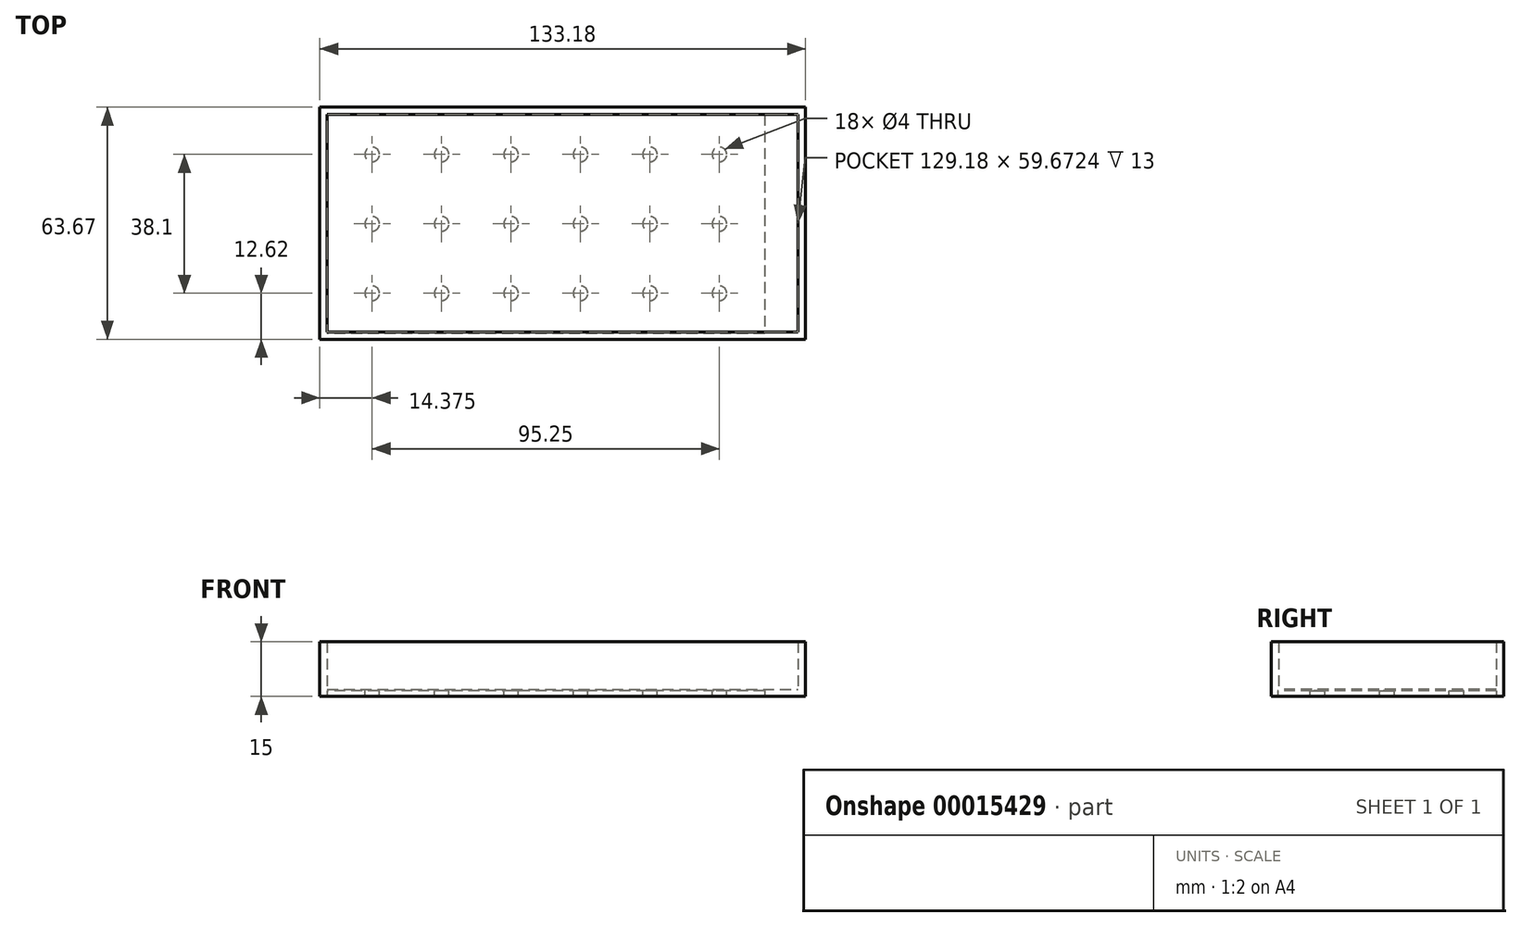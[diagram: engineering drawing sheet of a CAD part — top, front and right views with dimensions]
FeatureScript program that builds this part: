
annotation { "Feature Type Name" : "Feature", "Feature Type Description" : "" }
export const myFeature = defineFeature(function(context is Context, id is Id, definition is map)
    precondition{}
    {
        {
            var Q0;
            Q0=qCreatedBy(makeId("Top.planeOp"),FACE);
            var sketch = newSketch(context, id + "F0", { "sketchPlane" : qUnion([Q0])});
            skLineSegment(sketch, "E0.rect.bottom", {"start": v(60, 30) * mm, "end": v(-60, 30) * mm});
            skLineSegment(sketch, "E0.rect.top", {"start": v(60, -30) * mm, "end": v(-60, -30) * mm});
            skLineSegment(sketch, "E0.rect.left", {"start": v(60, 30) * mm, "end": v(60, -30) * mm});
            skLineSegment(sketch, "E0.rect.right", {"start": v(-60, 30) * mm, "end": v(-60, -30) * mm});
            skPoint(sketch, "E0.rect.middle", {"position": v(0, 0) * mm});
            skSolve(sketch);
        }
        {
            var Q0;
            Q0=qSketchRegion(id+"F0",true);
            extrude(context, id + "F1", {"entities" : qUnion([Q0]), "depth" : 1.6 * mm});
        }
        {
            var Q0;
            Q0=makeQuery(id+"F1.opExtrude","CAP_FACE",FACE,{"disambiguationData":[OSD([sQuery(id+"F0.wireOp",EDGE,"E0.rect.bottom"),sQuery(id+"F0.wireOp",EDGE,"E0.rect.top"),sQuery(id+"F0.wireOp",EDGE,"E0.rect.left"),sQuery(id+"F0.wireOp",EDGE,"E0.rect.right")])],"isStart":false});
            var sketch = newSketch(context, id + "F2", { "sketchPlane" : qUnion([Q0])});
            skCircle(sketch, "E1", {"center": v(-47.62, 19.05) * mm, "radius": 2 * mm});
            skCircle(sketch, "E2.0.1.0", {"center": v(-47.62, 0) * mm, "radius": 2 * mm});
            skCircle(sketch, "E2.0.2.0", {"center": v(-47.62, -19.05) * mm, "radius": 2 * mm});
            skCircle(sketch, "E2.1.0.0", {"center": v(-28.57, 19.05) * mm, "radius": 2 * mm});
            skCircle(sketch, "E2.1.1.0", {"center": v(-28.57, 0) * mm, "radius": 2 * mm});
            skCircle(sketch, "E2.1.2.0", {"center": v(-28.57, -19.05) * mm, "radius": 2 * mm});
            skCircle(sketch, "E2.2.0.0", {"center": v(-9.52, 19.05) * mm, "radius": 2 * mm});
            skCircle(sketch, "E2.2.1.0", {"center": v(-9.52, 0) * mm, "radius": 2 * mm});
            skCircle(sketch, "E2.2.2.0", {"center": v(-9.52, -19.05) * mm, "radius": 2 * mm});
            skCircle(sketch, "E2.3.0.0", {"center": v(9.53, 19.05) * mm, "radius": 2 * mm});
            skCircle(sketch, "E2.3.1.0", {"center": v(9.53, 0) * mm, "radius": 2 * mm});
            skCircle(sketch, "E2.3.2.0", {"center": v(9.53, -19.05) * mm, "radius": 2 * mm});
            skCircle(sketch, "E2.4.0.0", {"center": v(28.58, 19.05) * mm, "radius": 2 * mm});
            skCircle(sketch, "E2.4.1.0", {"center": v(28.58, 0) * mm, "radius": 2 * mm});
            skCircle(sketch, "E2.4.2.0", {"center": v(28.58, -19.05) * mm, "radius": 2 * mm});
            skCircle(sketch, "E2.5.0.0", {"center": v(47.62, 19.05) * mm, "radius": 2 * mm});
            skCircle(sketch, "E2.5.1.0", {"center": v(47.62, 0) * mm, "radius": 2 * mm});
            skCircle(sketch, "E2.5.2.0", {"center": v(47.62, -19.05) * mm, "radius": 2 * mm});
            skLineSegment(sketch, "E2.direction1", {"start": v(-47.62, 19.05) * mm, "end": v(-28.57, 19.05) * mm, "construction": true});
            skLineSegment(sketch, "E2.direction2", {"start": v(-47.62, 19.05) * mm, "end": v(-47.62, 0) * mm, "construction": true});
            skSolve(sketch);
        }
        {
            var Q0;
            Q0=qSketchRegion(id+"F2",true);
            extrude(context, id + "F3", {"entities" : qUnion([Q0]), "operationType" : NewBodyOperationType.REMOVE, "oppositeDirection" : true, "depth" : 25 * mm});
        }
        {
            var Q0;
            Q0=qCreatedBy(makeId("Top.planeOp"),FACE);
            var sketch = newSketch(context, id + "F4", { "sketchPlane" : qUnion([Q0])});
            skLineSegment(sketch, "E3.bottom", {"start": v(-62, 32) * mm, "end": v(71.18, 32) * mm});
            skLineSegment(sketch, "E3.top", {"start": v(-62, -31.67) * mm, "end": v(71.18, -31.67) * mm});
            skLineSegment(sketch, "E3.left", {"start": v(-62, 32) * mm, "end": v(-62, -31.67) * mm});
            skLineSegment(sketch, "E3.right", {"start": v(71.18, 32) * mm, "end": v(71.18, -31.67) * mm});
            skSolve(sketch);
        }
        {
            var Q0;
            Q0=qSketchRegion(id+"F4",true);
            extrude(context, id + "F5", {"entities" : qUnion([Q0]), "depth" : 15 * mm});
        }
        {
            var Q0;
            Q0=makeQuery(id+"F5.opExtrude","CAP_FACE",FACE,{"disambiguationData":[OSD([sQuery(id+"F4.wireOp",EDGE,"E3.bottom"),sQuery(id+"F4.wireOp",EDGE,"E3.top"),sQuery(id+"F4.wireOp",EDGE,"E3.left"),sQuery(id+"F4.wireOp",EDGE,"E3.right")])],"isStart":false});
            shell(context, id + "F6", {"entities" : qUnion([Q0]), "thickness" : 2 * mm});
        }
    });
